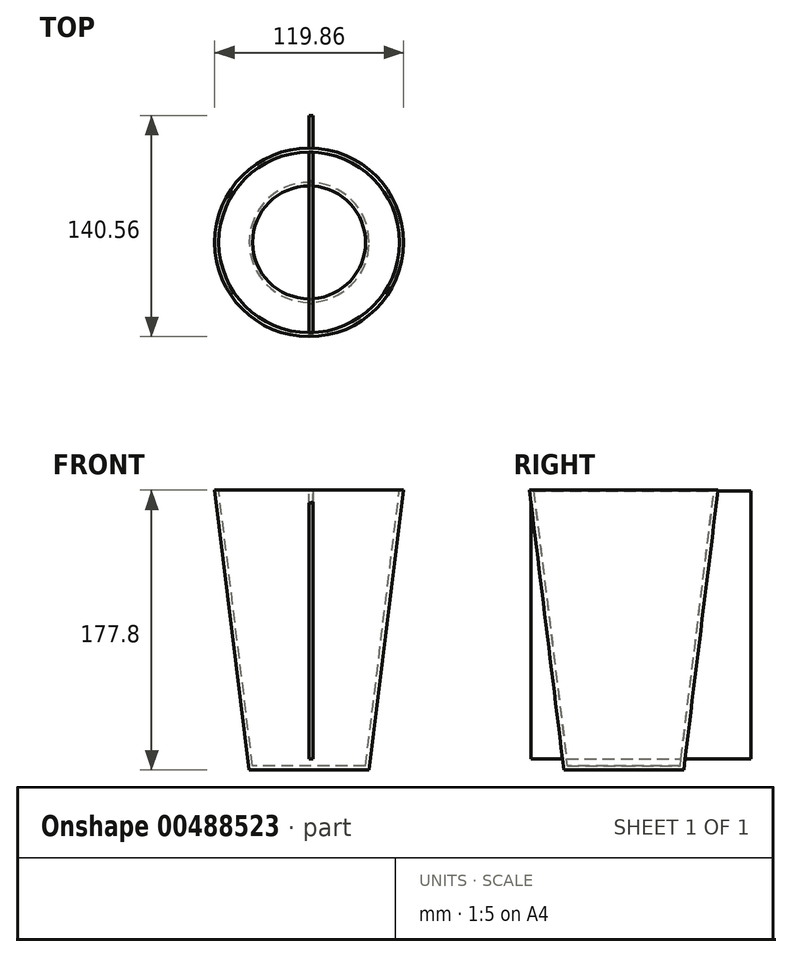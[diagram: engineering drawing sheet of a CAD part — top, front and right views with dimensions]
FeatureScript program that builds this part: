
annotation { "Feature Type Name" : "Feature", "Feature Type Description" : "" }
export const myFeature = defineFeature(function(context is Context, id is Id, definition is map)
    precondition{}
    {
        {
            var Q0;
            Q0=qCreatedBy(makeId("Top.planeOp"),FACE);
            var sketch = newSketch(context, id + "F0", { "sketchPlane" : qUnion([Q0])});
            skCircle(sketch, "E0", {"center": v(0, 0) * mm, "radius": 38.1 * mm});
            skSolve(sketch);
        }
        {
            var Q0;
            Q0=makeQuery(id+"F0.imprint","IMPRINT",FACE,{"disambiguationData":[TD([[makeQuery(id+"F0.imprint","IMPRINT",EDGE,{"derivedFrom":sQuery(id+"F0.wireOp",EDGE,"E0")}),1.0]])]});
            var Q1;
            Q1 = qSketchRegion(id + "FUW06tvp2SUNUul_1", true);
            extrude(context, id + "F1", {"entities" : qUnion([Q0, Q1]), "depth" : 177.8 * mm, "hasDraft" : true, "draftAngle" : 7 * degree});
        }
        {
            var Q0;
            Q0=makeQuery(id+"F1.opExtrude","CAP_FACE",FACE,{"disambiguationData":[OSD([sQuery(id+"F0.wireOp",EDGE,"E0")])],"isStart":false});
            shell(context, id + "F2", {"entities" : qUnion([Q0]), "thickness" : 2.54 * mm});
        }
        {
            var Q0;
            Q0=qCreatedBy(makeId("Right.planeOp"),FACE);
            var sketch = newSketch(context, id + "F3", { "sketchPlane" : qUnion([Q0])});
            skLineSegment(sketch, "E1.bottom", {"start": v(-58.94, 177.43) * mm, "end": v(80.63, 177.43) * mm});
            skLineSegment(sketch, "E1.top", {"start": v(-58.94, 7) * mm, "end": v(80.63, 7) * mm});
            skLineSegment(sketch, "E1.left", {"start": v(-58.94, 177.43) * mm, "end": v(-58.94, 7) * mm});
            skLineSegment(sketch, "E1.right", {"start": v(80.63, 177.43) * mm, "end": v(80.63, 7) * mm});
            skSolve(sketch);
        }
        {
            var Q0;
            Q0 = qSketchRegion(id + "F3", true);
            extrude(context, id + "F4", {"entities" : qUnion([Q0]), "operationType" : NewBodyOperationType.ADD, "depth" : 2.54 * mm});
        }
    });
